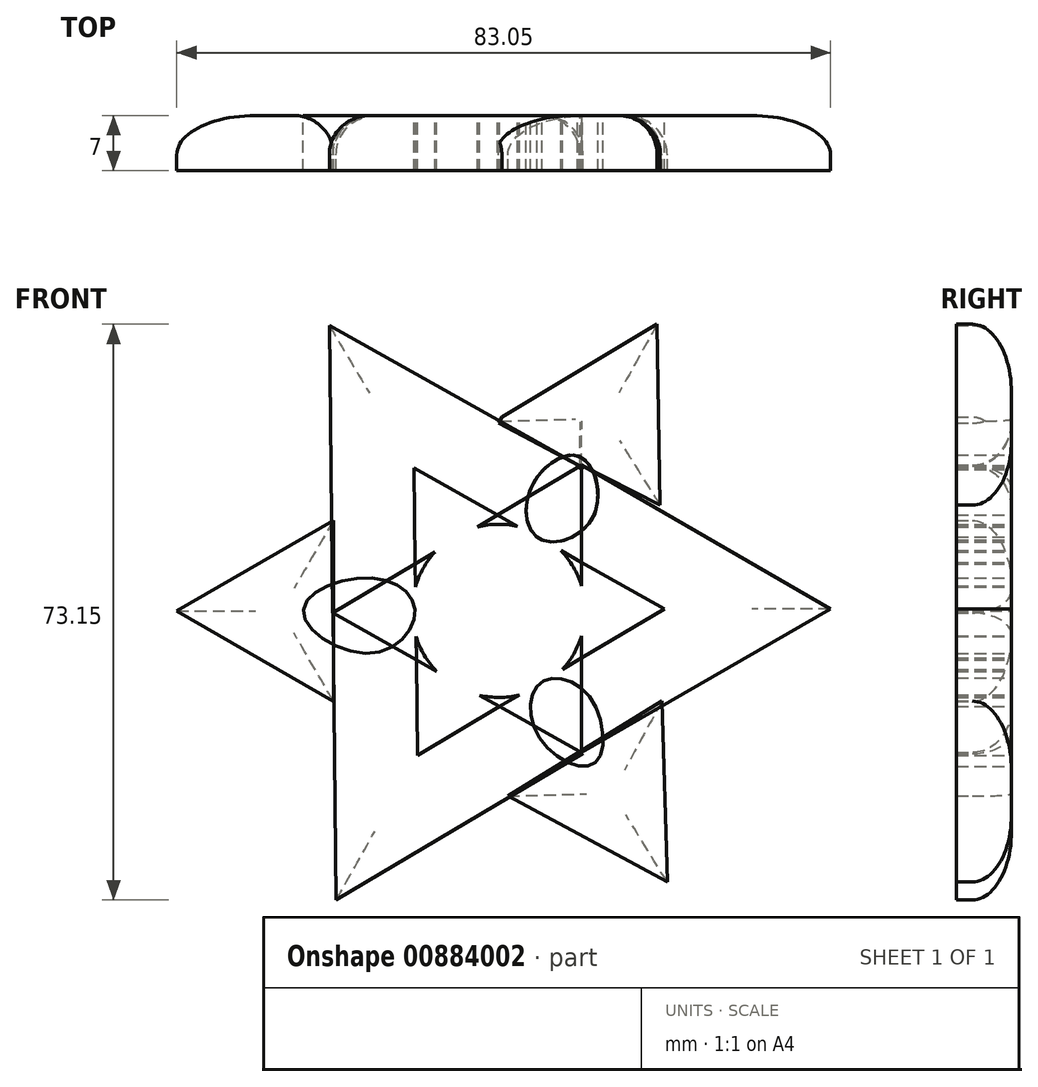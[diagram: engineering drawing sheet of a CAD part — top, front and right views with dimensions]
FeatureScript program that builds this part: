
annotation { "Feature Type Name" : "Feature", "Feature Type Description" : "" }
export const myFeature = defineFeature(function(context is Context, id is Id, definition is map)
    precondition{}
    {
        {
            var Q0;
            Q0=qCreatedBy(makeId("Front.planeOp"),FACE);
            var sketch = newSketch(context, id + "F0", { "sketchPlane" : qUnion([Q0])});
            skCircle(sketch, "E0.cCircle", {"center": v(0, 0) * mm, "radius": 10.54 * mm, "construction": true});
            skLineSegment(sketch, "E0.0", {"start": v(-10.75, 18.12) * mm, "end": v(21.07, 0.25) * mm});
            skLineSegment(sketch, "E0.1", {"start": v(21.07, 0.25) * mm, "end": v(-10.32, -18.37) * mm});
            skLineSegment(sketch, "E0.2", {"start": v(-10.32, -18.37) * mm, "end": v(-10.75, 18.12) * mm});
            skPoint(sketch, "E0.0.midPoint", {"position": v(5.16, 9.19) * mm});
            skCircle(sketch, "E1.cCircle", {"center": v(21.07, 0.25) * mm, "radius": 10.54 * mm, "construction": true});
            skLineSegment(sketch, "E1.0", {"start": v(10.53, -18) * mm, "end": v(10.53, 18.5) * mm});
            skLineSegment(sketch, "E1.1", {"start": v(10.53, 18.5) * mm, "end": v(42.15, 0.25) * mm});
            skLineSegment(sketch, "E1.2", {"start": v(42.15, 0.25) * mm, "end": v(10.53, -18) * mm});
            skPoint(sketch, "E1.0.midPoint", {"position": v(10.53, 0.25) * mm});
            skCircle(sketch, "E2.cCircle", {"center": v(-10.75, 18.12) * mm, "radius": 10.54 * mm, "construction": true});
            skLineSegment(sketch, "E2.0", {"start": v(10.32, 18.37) * mm, "end": v(-21.07, -0.25) * mm});
            skLineSegment(sketch, "E2.1", {"start": v(-21.07, -0.25) * mm, "end": v(-21.5, 36.25) * mm});
            skLineSegment(sketch, "E2.2", {"start": v(-21.5, 36.25) * mm, "end": v(10.32, 18.37) * mm});
            skPoint(sketch, "E2.0.midPoint", {"position": v(-5.38, 9.06) * mm});
            skCircle(sketch, "E3.cCircle", {"center": v(-10.32, -18.37) * mm, "radius": 10.53 * mm, "construction": true});
            skLineSegment(sketch, "E3.0", {"start": v(-20.63, -36.73) * mm, "end": v(-21.06, -0.27) * mm});
            skLineSegment(sketch, "E3.1", {"start": v(-21.06, -0.27) * mm, "end": v(10.73, -18.12) * mm});
            skLineSegment(sketch, "E3.2", {"start": v(10.73, -18.12) * mm, "end": v(-20.63, -36.73) * mm});
            skPoint(sketch, "E3.0.midPoint", {"position": v(-20.84, -18.5) * mm});
            skSolve(sketch);
        }
        {
            var Q0;
            {var subQ0=sQuery(id+"F0.wireOp",EDGE,"E2.1");Q0=makeQuery(id+"F0.imprint","IMPRINT",FACE,{"disambiguationData":[TD([[makeQuery(id+"F0.imprint","IMPRINT",EDGE,{"derivedFrom":subQ0}),-1.0]])]});}
            var Q1;
            {var subQ1=sQuery(id+"F0.wireOp",EDGE,"E0.0");var subQ9=sQuery(id+"F0.wireOp",EDGE,"E2.0");var subQ11=makeQuery(id+"F0.imprint","INTERSECT",VERTEX,{"derivedFrom":[subQ1,subQ9]});Q1=makeQuery(id+"F0.imprint","IMPRINT",FACE,{"disambiguationData":[TD([[makeQuery(id+"F0.imprint","IMPRINT",EDGE,{"disambiguationData":[TD([[subQ11,-1.0]])],"derivedFrom":subQ1}),-1.0]])]});}
            var Q2;
            {var subQ0=sQuery(id+"F0.wireOp",EDGE,"E1.1");Q2=makeQuery(id+"F0.imprint","IMPRINT",FACE,{"disambiguationData":[TD([[makeQuery(id+"F0.imprint","IMPRINT",EDGE,{"derivedFrom":subQ0}),-1.0]])]});}
            var Q3;
            {var subQ0=sQuery(id+"F0.wireOp",EDGE,"E3.0");Q3=makeQuery(id+"F0.imprint","IMPRINT",FACE,{"disambiguationData":[TD([[makeQuery(id+"F0.imprint","IMPRINT",EDGE,{"derivedFrom":subQ0}),-1.0]])]});}
            extrude(context, id + "F1", {"entities" : qUnion([Q0, Q1, Q2, Q3]), "depth" : 7 * mm, "offsetDistance" : 25 * mm});
        }
        {
            var Q0;
            {var subQ1=sQuery(id+"F0.wireOp",EDGE,"E0.0");var subQ9=sQuery(id+"F0.wireOp",EDGE,"E2.0");var subQ11=makeQuery(id+"F0.imprint","INTERSECT",VERTEX,{"derivedFrom":[subQ1,subQ9]});Q0=makeQuery(id+"F0.imprint","IMPRINT",FACE,{"disambiguationData":[TD([[makeQuery(id+"F0.imprint","IMPRINT",EDGE,{"disambiguationData":[TD([[subQ11,-1.0]])],"derivedFrom":subQ1}),-1.0]])]});}
            var sketch = newSketch(context, id + "F2", { "sketchPlane" : qUnion([Q0])});
            skCircle(sketch, "E4", {"center": v(0, 0) * mm, "radius": 11 * mm});
            skSolve(sketch);
        }
        {
            var Q0;
            Q0=makeQuery(id+"F2.imprint","IMPRINT",FACE,{"disambiguationData":[TD([[makeQuery(id+"F2.imprint","IMPRINT",EDGE,{"derivedFrom":sQuery(id+"F2.wireOp",EDGE,"E4")}),1.0]])]});
            extrude(context, id + "F3", {"entities" : qUnion([Q0]), "operationType" : NewBodyOperationType.REMOVE, "depth" : 51.8 * mm, "offsetDistance" : 25 * mm});
        }
        {
            var Q0;
            Q0=makeQuery(id+"F1.opExtrude","CAP_EDGE",EDGE,{"disambiguationData":[OSD([sQuery(id+"F0.wireOp",EDGE,"E2.2")])],"isStart":true});
            var Q1;
            Q1=makeQuery(id+"F1.opExtrude","CAP_EDGE",EDGE,{"disambiguationData":[OSD([sQuery(id+"F0.wireOp",EDGE,"E2.1")])],"isStart":true});
            var Q2;
            Q2=makeQuery(id+"F1.opExtrude","CAP_EDGE",EDGE,{"disambiguationData":[OSD([sQuery(id+"F0.wireOp",EDGE,"E3.0")])],"isStart":true});
            var Q3;
            Q3=makeQuery(id+"F1.opExtrude","CAP_EDGE",EDGE,{"disambiguationData":[OSD([sQuery(id+"F0.wireOp",EDGE,"E3.2")])],"isStart":true});
            var Q4;
            Q4=makeQuery(id+"F1.opExtrude","CAP_EDGE",EDGE,{"disambiguationData":[OSD([sQuery(id+"F0.wireOp",EDGE,"E1.2")])],"isStart":true});
            var Q5;
            Q5=makeQuery(id+"F1.opExtrude","CAP_EDGE",EDGE,{"disambiguationData":[OSD([sQuery(id+"F0.wireOp",EDGE,"E1.1")])],"isStart":true});
            fillet(context, id + "F4", {"entities" : qUnion([Q0, Q1, Q2, Q3, Q4, Q5]), "tangentPropagation" : true, "radius" : 5 * mm, "defaultsChanged" : false, "vertexSettings" : [], "allowEdgeOverflow" : false});
        }
        {
            var Q0;
            Q0=qCreatedBy(makeId("Front.planeOp"),FACE);
            var sketch = newSketch(context, id + "F5", { "sketchPlane" : qUnion([Q0])});
            skCircle(sketch, "E5.cCircle", {"center": v(-27.62, 0) * mm, "radius": 6.64 * mm, "construction": true});
            skLineSegment(sketch, "E5.0", {"start": v(-20.98, 11.5) * mm, "end": v(-20.98, -11.5) * mm});
            skLineSegment(sketch, "E5.1", {"start": v(-20.98, -11.5) * mm, "end": v(-40.9, 0) * mm});
            skLineSegment(sketch, "E5.2", {"start": v(-40.9, 0) * mm, "end": v(-20.98, 11.5) * mm});
            skPoint(sketch, "E5.0.midPoint", {"position": v(-20.98, 0) * mm});
            skCircle(sketch, "E6.cCircle", {"center": v(13.69, 24.81) * mm, "radius": 6.64 * mm, "construction": true});
            skLineSegment(sketch, "E6.0", {"start": v(20.52, 13.42) * mm, "end": v(0.4, 24.6) * mm});
            skLineSegment(sketch, "E6.1", {"start": v(0.4, 24.6) * mm, "end": v(20.14, 36.42) * mm});
            skLineSegment(sketch, "E6.2", {"start": v(20.14, 36.42) * mm, "end": v(20.52, 13.42) * mm});
            skPoint(sketch, "E6.0.midPoint", {"position": v(10.46, 19) * mm});
            skLineSegment(sketch, "E7", {"start": v(0.4, 24.6) * mm, "end": v(10.3, 18.4) * mm});
            skLineSegment(sketch, "E8", {"start": v(10.3, 18.4) * mm, "end": v(10.52, 18.5) * mm});
            skLineSegment(sketch, "E9", {"start": v(10.52, 18.5) * mm, "end": v(20.52, 13.42) * mm});
            skLineSegment(sketch, "E10", {"start": v(0.4, 24.6) * mm, "end": v(0, 23.86) * mm});
            skLineSegment(sketch, "E11", {"start": v(0, 23.86) * mm, "end": v(10.3, 18.4) * mm});
            skLineSegment(sketch, "E12", {"start": v(20.52, 13.42) * mm, "end": v(20.03, 12.47) * mm});
            skLineSegment(sketch, "E13", {"start": v(20.03, 12.47) * mm, "end": v(10.3, 18.4) * mm});
            skSolve(sketch);
        }
        {
            var Q0;
            Q0=qCreatedBy(makeId("Front.planeOp"),FACE);
            var sketch = newSketch(context, id + "F6", { "sketchPlane" : qUnion([Q0])});
            skCircle(sketch, "E14.cCircle", {"center": v(14.44, -23.15) * mm, "radius": 6.64 * mm, "construction": true});
            skLineSegment(sketch, "E14.0", {"start": v(1.16, -23.54) * mm, "end": v(20.73, -11.45) * mm});
            skLineSegment(sketch, "E14.1", {"start": v(20.73, -11.45) * mm, "end": v(21.41, -34.44) * mm});
            skLineSegment(sketch, "E14.2", {"start": v(21.41, -34.44) * mm, "end": v(1.16, -23.54) * mm});
            skPoint(sketch, "E14.0.midPoint", {"position": v(10.95, -17.5) * mm});
            skSolve(sketch);
        }
        {
            var Q0;
            Q0=qCreatedBy(makeId("Front.planeOp"),FACE);
            var sketch = newSketch(context, id + "F7", { "sketchPlane" : qUnion([Q0])});
            skLineSegment(sketch, "E15", {"start": v(10.02, 18.35) * mm, "end": v(10.64, 17.97) * mm});
            skLineSegment(sketch, "E16", {"start": v(10.64, 17.97) * mm, "end": v(10.52, 18.49) * mm});
            skLineSegment(sketch, "E17", {"start": v(10.52, 18.49) * mm, "end": v(10.02, 18.35) * mm});
            skSolve(sketch);
        }
        {
            var Q0;
            Q0=makeQuery(id+"F5.imprint","IMPRINT",FACE,{"disambiguationData":[TD([[makeQuery(id+"F5.imprint","IMPRINT",EDGE,{"derivedFrom":sQuery(id+"F5.wireOp",EDGE,"E5.0")}),-1.0]])]});
            var Q1;
            Q1=makeQuery(id+"F5.imprint","IMPRINT",FACE,{"disambiguationData":[TD([[makeQuery(id+"F5.imprint","IMPRINT",EDGE,{"derivedFrom":sQuery(id+"F5.wireOp",EDGE,"E6.0")}),-1.0]])]});
            var Q2;
            Q2=makeQuery(id+"F7.imprint","IMPRINT",FACE,{"disambiguationData":[TD([[makeQuery(id+"F7.imprint","IMPRINT",EDGE,{"derivedFrom":sQuery(id+"F7.wireOp",EDGE,"E15")}),1.0]])]});
            var Q3;
            Q3=makeQuery(id+"F5.imprint","IMPRINT",FACE,{"disambiguationData":[TD([[makeQuery(id+"F5.imprint","IMPRINT",EDGE,{"derivedFrom":sQuery(id+"F5.wireOp",EDGE,"E6.0")}),1.0]])]});
            var Q4;
            Q4=makeQuery(id+"F5.imprint","IMPRINT",FACE,{"disambiguationData":[TD([[makeQuery(id+"F5.imprint","IMPRINT",EDGE,{"derivedFrom":sQuery(id+"F5.wireOp",EDGE,"E7")}),-1.0]])]});
            extrude(context, id + "F8", {"entities" : qUnion([Q0, Q1, Q2, Q3, Q4]), "depth" : 7 * mm, "offsetDistance" : 25 * mm});
        }
        {
            var Q0;
            Q0=makeQuery(id+"F6.imprint","IMPRINT",FACE,{"disambiguationData":[TD([[makeQuery(id+"F6.imprint","IMPRINT",EDGE,{"derivedFrom":sQuery(id+"F6.wireOp",EDGE,"E14.0")}),-1.0]])]});
            extrude(context, id + "F9", {"entities" : qUnion([Q0]), "depth" : 7 * mm, "offsetDistance" : 25 * mm});
        }
        {
            var Q0;
            Q0=makeQuery(id+"F8.opExtrude","CAP_FACE",FACE,{"disambiguationData":[OSD([sQuery(id+"F5.wireOp",EDGE,"E5.0"),sQuery(id+"F5.wireOp",EDGE,"E5.1"),sQuery(id+"F5.wireOp",EDGE,"E5.2")])],"isStart":true});
            var Q1;
            Q1=makeQuery(id+"F8.opExtrude","CAP_FACE",FACE,{"disambiguationData":[OSD([sQuery(id+"F5.wireOp",EDGE,"E6.1"),sQuery(id+"F5.wireOp",EDGE,"E6.2"),sQuery(id+"F5.wireOp",EDGE,"E8"),sQuery(id+"F5.wireOp",EDGE,"E9"),sQuery(id+"F5.wireOp",EDGE,"E10"),sQuery(id+"F5.wireOp",EDGE,"E11")])],"isStart":true});
            var Q2;
            Q2=makeQuery(id+"F9.opExtrude","CAP_EDGE",EDGE,{"disambiguationData":[OSD([sQuery(id+"F6.wireOp",EDGE,"E14.1")])],"isStart":true});
            var Q3;
            Q3=makeQuery(id+"F9.opExtrude","CAP_FACE",FACE,{"disambiguationData":[OSD([sQuery(id+"F6.wireOp",EDGE,"E14.0"),sQuery(id+"F6.wireOp",EDGE,"E14.1"),sQuery(id+"F6.wireOp",EDGE,"E14.2")])],"isStart":true});
            fillet(context, id + "F10", {"entities" : qUnion([Q0, Q1, Q2, Q3]), "tangentPropagation" : true, "radius" : 5 * mm, "defaultsChanged" : false, "vertexSettings" : [], "allowEdgeOverflow" : false});
        }
        {
            var Q0;
            Q0=qCreatedBy(makeId("Front.planeOp"),FACE);
            var sketch = newSketch(context, id + "F11", { "sketchPlane" : qUnion([Q0])});
            skFitSpline(sketch, "E18", {"points": [v(-11.5, 11.36) * mm, v(-5.56, 9.13) * mm, v(-4.06, 16.11) * mm, v(-10.68, 20.1) * mm, v(-11.5, 11.36) * mm]});
            skFitSpline(sketch, "E19", {"points": [v(4.17, 15.75) * mm, v(5.2, 9.13) * mm, v(11.98, 11.87) * mm, v(10.33, 19.58) * mm, v(4.17, 15.75) * mm]});
            skFitSpline(sketch, "E20", {"points": [v(16.12, 4.29) * mm, v(10.56, 0) * mm, v(15.98, -4.7) * mm, v(24.67, 0) * mm, v(16.12, 4.29) * mm]});
            skFitSpline(sketch, "E21", {"points": [v(5.16, -16.14) * mm, v(5.31, -9.15) * mm, v(11.42, -10.76) * mm, v(12.2, -19.35) * mm, v(5.16, -16.14) * mm]});
            skFitSpline(sketch, "E22", {"points": [v(-11.5, -12.36) * mm, v(-4.93, -9.41) * mm, v(-4.72, -16.7) * mm, v(-11.5, -20.28) * mm, v(-11.5, -12.36) * mm]});
            skFitSpline(sketch, "E23", {"points": [v(-16.1, 4.18) * mm, v(-10.63, 0) * mm, v(-16.2, -5.4) * mm, v(-24.83, 0) * mm, v(-16.1, 4.18) * mm]});
            skSolve(sketch);
        }
        {
            var Q0;
            Q0=makeQuery(id+"F11.imprint","IMPRINT",FACE,{"disambiguationData":[TD([[makeQuery(id+"F11.imprint","IMPRINT",EDGE,{"derivedFrom":sQuery(id+"F11.wireOp",EDGE,"E23")}),-1.0]])]});
            var Q1;
            Q1=makeQuery(id+"F11.imprint","IMPRINT",FACE,{"disambiguationData":[TD([[makeQuery(id+"F11.imprint","IMPRINT",EDGE,{"derivedFrom":sQuery(id+"F11.wireOp",EDGE,"E19")}),1.0]])]});
            var Q2;
            Q2=makeQuery(id+"F11.imprint","IMPRINT",FACE,{"disambiguationData":[TD([[makeQuery(id+"F11.imprint","IMPRINT",EDGE,{"derivedFrom":sQuery(id+"F11.wireOp",EDGE,"E21")}),-1.0]])]});
            extrude(context, id + "F12", {"entities" : qUnion([Q0, Q1, Q2]), "depth" : 7 * mm, "offsetDistance" : 25 * mm});
        }
    });
